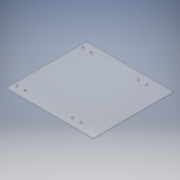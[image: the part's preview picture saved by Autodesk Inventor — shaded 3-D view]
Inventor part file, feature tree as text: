
AUTODESK INVENTOR PART (.ipt)
format: ipt  version: 2019 (Build 230136000, 136)  size: 124,416 bytes
history: native  units: in
note: dims shown in document units (in); Inventor stores cm internally (conversion verified against a paired STEP export)
features: sketch x2, extrude x1, hole x1, projected_geometry x1
ambient origin geometry x8: Origin, YZ Plane, XZ Plane, XY Plane, X Axis, Y Axis, Z Axis, Center Point
bodies: Solid1 (feature_tree)
feature tree (5):
  extrude  "Extrusion1"  Depth=6.0in
  hole  "Hole1"  [1 undecoded]
  sketch  "Sketch1"  dims[d0=6.5in d1=6.0in]
  sketch  "Sketch2"  dims[d2=0.073in d3=0.0in d4=6.5in d5=0.6299in d6=0.6299in d7=0.6299in d8=0.6299in d9=0.557in d10=0.557in d11=0.557in d12=0.557in d13=0.557in d14=0.557in d15=0.557in d16=0.557in d17=2.097in d18=2.097in d19=6.23in d20=6.23in d21=0.15in d22=0.75in d23=0.375in d24=0.25in d25=0.5635in d26=0.432in d27=0.8108in]
  projected_geometry  "Projected Loop1"
note: 1 required parameter value undecoded (feature->parameter linkage not recoverable at this tier; creation-order binding heuristic only, values carry confidence <= 0.55)
